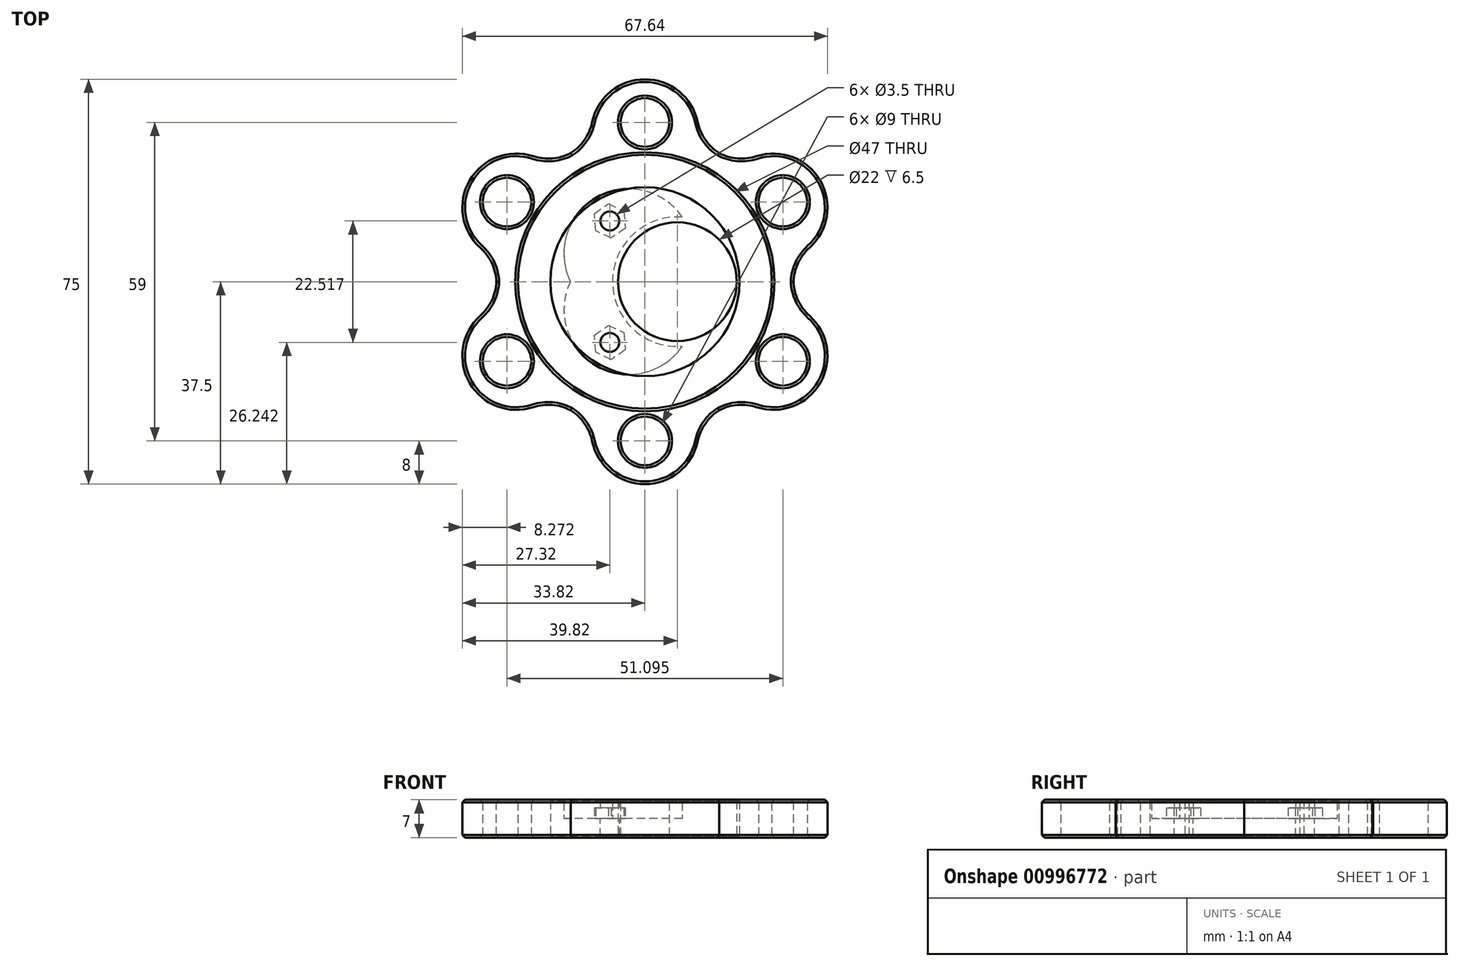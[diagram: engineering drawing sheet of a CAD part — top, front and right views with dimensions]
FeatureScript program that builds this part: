
annotation { "Feature Type Name" : "Feature", "Feature Type Description" : "" }
export const myFeature = defineFeature(function(context is Context, id is Id, definition is map)
    precondition{}
    {
        {
            var Q0;
            Q0=qCreatedBy(makeId("Top.planeOp"),FACE);
            var sketch = newSketch(context, id + "F0", { "sketchPlane" : qUnion([Q0])});
            skCircle(sketch, "E0", {"center": v(0, 0) * mm, "radius": 17.5 * mm});
            skCircle(sketch, "E1", {"center": v(6, 0) * mm, "radius": 11 * mm});
            skLineSegment(sketch, "E2", {"start": v(0, 0) * mm, "end": v(13.77, 19.66) * mm});
            skLineSegment(sketch, "E3", {"start": v(0, 0) * mm, "end": v(14.89, -21.26) * mm});
            skSolve(sketch);
        }
        {
            var Q0;
            Q0=qSketchRegion(id+"F0",true);
            var Q1;
            {var subQ0=sQuery(id+"F0.wireOp",EDGE,"7888d7e4-cc9e-4509-8198-0eb2202acd58");var subQ1=sQuery(id+"F0.wireOp",EDGE,"E0");var subQ2=makeQuery(id+"F0.imprint","INTERSECT",VERTEX,{"derivedFrom":[subQ1,subQ0]});Q1=makeQuery(id+"F0.imprint","IMPRINT",FACE,{"disambiguationData":[TD([[makeQuery(id+"F0.imprint","IMPRINT",EDGE,{"disambiguationData":[TD([[subQ2,1.0]])],"derivedFrom":subQ1}),1.0]])]});}
            extrude(context, id + "F1", {"entities" : qUnion([Q0, Q1]), "depth" : 3.25 * mm, "offsetDistance" : 25 * mm, "hasSecondDirection" : true, "secondDirectionOppositeDirection" : true, "secondDirectionDepth" : 3.25 * mm});
        }
        {
            var Q0;
            Q0=qCreatedBy(makeId("Top.planeOp"),FACE);
            var sketch = newSketch(context, id + "F2", { "sketchPlane" : qUnion([Q0])});
            skCircle(sketch, "E4", {"center": v(0, 0) * mm, "radius": 23.5 * mm});
            skArc(sketch, "E5", {"start": v(-3.88, 27.22) * mm, "mid": v(-13.75, 23.82) * mm, "end": v(-21.64, 16.97) * mm});
            skArc(sketch, "E6", {"start": v(9.83, 25.68) * mm, "mid": v(0, 37.5) * mm, "end": v(-9.83, 25.68) * mm});
            skArc(sketch, "E7.1.0", {"start": v(-17.32, 21.36) * mm, "mid": v(-32.48, 18.75) * mm, "end": v(-27.16, 4.33) * mm});
            skArc(sketch, "E7.2.0", {"start": v(-27.16, -4.33) * mm, "mid": v(-32.48, -18.75) * mm, "end": v(-17.32, -21.36) * mm});
            skArc(sketch, "E7.3.0", {"start": v(-9.83, -25.68) * mm, "mid": v(0, -37.5) * mm, "end": v(9.83, -25.68) * mm});
            skArc(sketch, "E7.4.0", {"start": v(17.32, -21.36) * mm, "mid": v(32.48, -18.75) * mm, "end": v(27.16, -4.33) * mm});
            skArc(sketch, "E7.5.0", {"start": v(27.16, 4.33) * mm, "mid": v(32.48, 18.75) * mm, "end": v(17.32, 21.36) * mm});
            skPoint(sketch, "E8.orphan", {"position": v(8.33, 21.97) * mm});
            skPoint(sketch, "E9.orphan", {"position": v(-8.33, 21.97) * mm});
            skPoint(sketch, "E10.orphan", {"position": v(-14.86, 18.2) * mm});
            skPoint(sketch, "E11.orphan", {"position": v(-23.2, 3.77) * mm});
            skPoint(sketch, "E12.orphan", {"position": v(-23.2, -3.77) * mm});
            skPoint(sketch, "E13.orphan", {"position": v(-14.86, -18.2) * mm});
            skPoint(sketch, "E14.orphan", {"position": v(-8.33, -21.97) * mm});
            skPoint(sketch, "E15.orphan", {"position": v(8.33, -21.97) * mm});
            skPoint(sketch, "E16.orphan", {"position": v(14.86, -18.2) * mm});
            skPoint(sketch, "E17.orphan", {"position": v(23.2, -3.77) * mm});
            skPoint(sketch, "E18.orphan", {"position": v(23.2, 3.77) * mm});
            skPoint(sketch, "E19.orphan", {"position": v(14.86, 18.2) * mm});
            skCircle(sketch, "E20", {"center": v(0, 29.5) * mm, "radius": 4.5 * mm});
            skCircle(sketch, "E21.1.0", {"center": v(-25.55, 14.75) * mm, "radius": 4.5 * mm});
            skCircle(sketch, "E21.2.0", {"center": v(-25.55, -14.75) * mm, "radius": 4.5 * mm});
            skCircle(sketch, "E21.3.0", {"center": v(0, -29.5) * mm, "radius": 4.5 * mm});
            skCircle(sketch, "E21.4.0", {"center": v(25.55, -14.75) * mm, "radius": 4.5 * mm});
            skCircle(sketch, "E21.5.0", {"center": v(25.55, 14.75) * mm, "radius": 4.5 * mm});
            skArc(sketch, "E22.trimOffspring", {"start": v(21.64, 16.97) * mm, "mid": v(13.75, 23.82) * mm, "end": v(3.88, 27.22) * mm});
            skArc(sketch, "E23.trimOffspring", {"start": v(25.52, -10.25) * mm, "mid": v(27.5, 0) * mm, "end": v(25.52, 10.25) * mm});
            skArc(sketch, "E24.trimOffspring", {"start": v(3.88, -27.22) * mm, "mid": v(13.75, -23.82) * mm, "end": v(21.64, -16.97) * mm});
            skArc(sketch, "E25.trimOffspring", {"start": v(-21.64, -16.97) * mm, "mid": v(-13.75, -23.82) * mm, "end": v(-3.88, -27.22) * mm});
            skArc(sketch, "E26.trimOffspring", {"start": v(-25.52, 10.25) * mm, "mid": v(-27.5, 0) * mm, "end": v(-25.52, -10.25) * mm});
            skSolve(sketch);
        }
        {
            var Q0;
            Q0=qSketchRegion(id+"F2",true);
            extrude(context, id + "F3", {"entities" : qUnion([Q0]), "depth" : 3.5 * mm, "offsetDistance" : 25 * mm, "hasSecondDirection" : true, "secondDirectionOppositeDirection" : true, "secondDirectionDepth" : 3.5 * mm});
        }
        {
            var Q0;
            {var subQ0=sQuery(id+"F2.wireOp",EDGE,"E7.1.0");var subQ1=sQuery(id+"F2.wireOp",EDGE,"E5");Q0=makeQuery(id+"F3.opExtrude","SWEPT_EDGE",EDGE,{"disambiguationData":[OSD([subQ1,subQ0]),TDD([makeQuery(id+"F2.imprint","INTERSECT",VERTEX,{"disambiguationData":[OD(0.0)],"derivedFrom":[subQ1,subQ0]})])]});}
            var Q1;
            {var subQ0=sQuery(id+"F2.wireOp",EDGE,"E6");var subQ1=sQuery(id+"F2.wireOp",EDGE,"E5");Q1=makeQuery(id+"F3.opExtrude","SWEPT_EDGE",EDGE,{"disambiguationData":[OSD([subQ1,subQ0]),TDD([makeQuery(id+"F2.imprint","INTERSECT",VERTEX,{"disambiguationData":[OD(1.0)],"derivedFrom":[subQ1,subQ0]})])]});}
            var Q2;
            {var subQ0=sQuery(id+"F2.wireOp",EDGE,"E7.1.0");var subQ1=sQuery(id+"F2.wireOp",EDGE,"E5");Q2=makeQuery(id+"F3.opExtrude","SWEPT_EDGE",EDGE,{"disambiguationData":[OSD([subQ1,subQ0]),TDD([makeQuery(id+"F2.imprint","INTERSECT",VERTEX,{"disambiguationData":[OD(1.0)],"derivedFrom":[subQ1,subQ0]})])]});}
            var Q3;
            {var subQ0=sQuery(id+"F2.wireOp",EDGE,"E7.2.0");var subQ1=sQuery(id+"F2.wireOp",EDGE,"E5");Q3=makeQuery(id+"F3.opExtrude","SWEPT_EDGE",EDGE,{"disambiguationData":[OSD([subQ1,subQ0]),TDD([makeQuery(id+"F2.imprint","INTERSECT",VERTEX,{"disambiguationData":[OD(0.0)],"derivedFrom":[subQ1,subQ0]})])]});}
            var Q4;
            {var subQ0=sQuery(id+"F2.wireOp",EDGE,"E7.2.0");var subQ1=sQuery(id+"F2.wireOp",EDGE,"E5");Q4=makeQuery(id+"F3.opExtrude","SWEPT_EDGE",EDGE,{"disambiguationData":[OSD([subQ1,subQ0]),TDD([makeQuery(id+"F2.imprint","INTERSECT",VERTEX,{"disambiguationData":[OD(1.0)],"derivedFrom":[subQ1,subQ0]})])]});}
            var Q5;
            {var subQ0=sQuery(id+"F2.wireOp",EDGE,"E7.3.0");var subQ1=sQuery(id+"F2.wireOp",EDGE,"E5");Q5=makeQuery(id+"F3.opExtrude","SWEPT_EDGE",EDGE,{"disambiguationData":[OSD([subQ1,subQ0]),TDD([makeQuery(id+"F2.imprint","INTERSECT",VERTEX,{"disambiguationData":[OD(0.0)],"derivedFrom":[subQ1,subQ0]})])]});}
            var Q6;
            {var subQ0=sQuery(id+"F2.wireOp",EDGE,"E7.3.0");var subQ1=sQuery(id+"F2.wireOp",EDGE,"E5");Q6=makeQuery(id+"F3.opExtrude","SWEPT_EDGE",EDGE,{"disambiguationData":[OSD([subQ1,subQ0]),TDD([makeQuery(id+"F2.imprint","INTERSECT",VERTEX,{"disambiguationData":[OD(1.0)],"derivedFrom":[subQ1,subQ0]})])]});}
            var Q7;
            {var subQ0=sQuery(id+"F2.wireOp",EDGE,"E7.4.0");var subQ1=sQuery(id+"F2.wireOp",EDGE,"E5");Q7=makeQuery(id+"F3.opExtrude","SWEPT_EDGE",EDGE,{"disambiguationData":[OSD([subQ1,subQ0]),TDD([makeQuery(id+"F2.imprint","INTERSECT",VERTEX,{"disambiguationData":[OD(0.0)],"derivedFrom":[subQ1,subQ0]})])]});}
            var Q8;
            {var subQ0=sQuery(id+"F2.wireOp",EDGE,"E7.4.0");var subQ1=sQuery(id+"F2.wireOp",EDGE,"E5");Q8=makeQuery(id+"F3.opExtrude","SWEPT_EDGE",EDGE,{"disambiguationData":[OSD([subQ1,subQ0]),TDD([makeQuery(id+"F2.imprint","INTERSECT",VERTEX,{"disambiguationData":[OD(1.0)],"derivedFrom":[subQ1,subQ0]})])]});}
            var Q9;
            {var subQ0=sQuery(id+"F2.wireOp",EDGE,"E7.5.0");var subQ1=sQuery(id+"F2.wireOp",EDGE,"E5");Q9=makeQuery(id+"F3.opExtrude","SWEPT_EDGE",EDGE,{"disambiguationData":[OSD([subQ1,subQ0]),TDD([makeQuery(id+"F2.imprint","INTERSECT",VERTEX,{"disambiguationData":[OD(0.0)],"derivedFrom":[subQ1,subQ0]})])]});}
            var Q10;
            {var subQ0=sQuery(id+"F2.wireOp",EDGE,"E7.5.0");var subQ1=sQuery(id+"F2.wireOp",EDGE,"E5");Q10=makeQuery(id+"F3.opExtrude","SWEPT_EDGE",EDGE,{"disambiguationData":[OSD([subQ1,subQ0]),TDD([makeQuery(id+"F2.imprint","INTERSECT",VERTEX,{"disambiguationData":[OD(1.0)],"derivedFrom":[subQ1,subQ0]})])]});}
            var Q11;
            {var subQ0=sQuery(id+"F2.wireOp",EDGE,"E6");var subQ1=sQuery(id+"F2.wireOp",EDGE,"E5");Q11=makeQuery(id+"F3.opExtrude","SWEPT_EDGE",EDGE,{"disambiguationData":[OSD([subQ1,subQ0]),TDD([makeQuery(id+"F2.imprint","INTERSECT",VERTEX,{"disambiguationData":[OD(0.0)],"derivedFrom":[subQ1,subQ0]})])]});}
            var Q12;
            Q12=makeQuery(id+"F3.opExtrude","SWEPT_EDGE",EDGE,{"disambiguationData":[OSD([sQuery(id+"F2.wireOp",EDGE,"E7.1.0"),sQuery(id+"F2.wireOp",EDGE,"E26.trimOffspring")])]});
            var Q13;
            Q13=makeQuery(id+"F3.opExtrude","SWEPT_EDGE",EDGE,{"disambiguationData":[OSD([sQuery(id+"F2.wireOp",EDGE,"E6"),sQuery(id+"F2.wireOp",EDGE,"E22.trimOffspring")])]});
            fillet(context, id + "F4", {"entities" : qUnion([Q0, Q1, Q2, Q3, Q4, Q5, Q6, Q7, Q8, Q9, Q10, Q11, Q12, Q13]), "tangentPropagation" : true, "radius" : 9 * mm, "defaultsChanged" : false, "vertexSettings" : [], "allowEdgeOverflow" : false});
        }
        {
            var Q0;
            Q0=qCreatedBy(makeId("Top.planeOp"),FACE);
            var sketch = newSketch(context, id + "F5", { "sketchPlane" : qUnion([Q0])});
            skLineSegment(sketch, "E27", {"start": v(0, -24.5) * mm, "end": v(35, 0) * mm});
            skLineSegment(sketch, "E28", {"start": v(35, 0) * mm, "end": v(0, 24.5) * mm});
            skSolve(sketch);
        }
        {
            var Q0;
            Q0=qSketchRegion(id+"F5",true);
            var Q1;
            Q1=sQuery(id+"F5.wireOp",EDGE,"E28");
            var Q2;
            Q2=sQuery(id+"F5.wireOp",EDGE,"E27");
            extrude(context, id + "F6", {"entities" : qUnion([Q0]), "bodyType" : ToolBodyType.SURFACE, "surfaceEntities" : qUnion([Q1, Q2]), "depth" : 3.5 * mm, "offsetDistance" : 25 * mm, "hasSecondDirection" : true, "secondDirectionOppositeDirection" : true, "secondDirectionDepth" : 3.5 * mm});
        }
        {
            var Q0;
            Q0=makeQuery(id+"F6.opExtrude","SWEPT_FACE",FACE,{"disambiguationData":[OSD([sQuery(id+"F5.wireOp",EDGE,"E28")])]});
            var sketch = newSketch(context, id + "F7", { "sketchPlane" : qUnion([Q0])});
            skPoint(sketch, "E29", {"position": v(0, 0) * mm});
            skSolve(sketch);
        }
        {
            var Q0;
            Q0=makeQuery(id+"F6.opExtrude","SWEPT_FACE",FACE,{"disambiguationData":[OSD([sQuery(id+"F5.wireOp",EDGE,"E27")])]});
            var sketch = newSketch(context, id + "F8", { "sketchPlane" : qUnion([Q0])});
            skPoint(sketch, "E30", {"position": v(0, 0) * mm});
            skSolve(sketch);
        }
        {
            var Q0;
            Q0=qCreatedBy(makeId("Top.planeOp"),FACE);
            var sketch = newSketch(context, id + "F9", { "sketchPlane" : qUnion([Q0])});
            skArc(sketch, "E31", {"start": v(6.9, 11.97) * mm, "mid": v(-6, 0) * mm, "end": v(6.9, -11.97) * mm});
            skArc(sketch, "E32.1.0", {"start": v(6.9, 11.97) * mm, "mid": v(-9, 15.59) * mm, "end": v(-13.82, 0) * mm});
            skArc(sketch, "E32.2.0", {"start": v(-13.82, 0) * mm, "mid": v(-9, -15.59) * mm, "end": v(6.9, -11.97) * mm});
            skPoint(sketch, "E32.center", {"position": v(0, 0) * mm});
            skLineSegment(sketch, "E33", {"start": v(-6.5, -11.26) * mm, "end": v(-3.9, -6.77) * mm});
            skLineSegment(sketch, "E34", {"start": v(-6.5, 11.26) * mm, "end": v(-3.9, 6.77) * mm});
            skSolve(sketch);
        }
        {
            var Q0;
            {var subQ0=sQuery(id+"F9.wireOp",EDGE,"E32.1.0");Q0=makeQuery(id+"F9.imprint","IMPRINT",FACE,{"disambiguationData":[TD([[makeQuery(id+"F9.imprint","IMPRINT",EDGE,{"derivedFrom":subQ0}),1.0]])]});}
            extrude(context, id + "F10", {"entities" : qUnion([Q0]), "depth" : 3 * mm, "offsetDistance" : 25 * mm});
        }
        {
            var Q0;
            {var subQ0=sQuery(id+"F9.wireOp",EDGE,"E32.1.0");Q0=makeQuery(id+"F9.imprint","IMPRINT",FACE,{"disambiguationData":[TD([[makeQuery(id+"F9.imprint","IMPRINT",EDGE,{"derivedFrom":subQ0}),1.0]])]});}
            var sketch = newSketch(context, id + "F11", { "sketchPlane" : qUnion([Q0])});
            skCircle(sketch, "E35.cCircle", {"center": v(-6.5, 11.26) * mm, "radius": 2.75 * mm, "construction": true});
            skLineSegment(sketch, "E35.0", {"start": v(-3.9, 13.07) * mm, "end": v(-3.63, 9.9) * mm});
            skLineSegment(sketch, "E35.1", {"start": v(-3.63, 9.9) * mm, "end": v(-6.24, 8.1) * mm});
            skLineSegment(sketch, "E35.2", {"start": v(-6.24, 8.1) * mm, "end": v(-9.1, 9.45) * mm});
            skLineSegment(sketch, "E35.3", {"start": v(-9.1, 9.45) * mm, "end": v(-9.37, 12.61) * mm});
            skLineSegment(sketch, "E35.4", {"start": v(-9.37, 12.61) * mm, "end": v(-6.76, 14.42) * mm});
            skLineSegment(sketch, "E35.5", {"start": v(-6.76, 14.42) * mm, "end": v(-3.9, 13.07) * mm});
            skPoint(sketch, "E35.0.midPoint", {"position": v(-3.76, 11.49) * mm});
            skCircle(sketch, "E36.cCircle", {"center": v(-6.5, -11.26) * mm, "radius": 2.75 * mm, "construction": true});
            skLineSegment(sketch, "E36.0", {"start": v(-3.9, -9.45) * mm, "end": v(-3.63, -12.61) * mm});
            skLineSegment(sketch, "E36.1", {"start": v(-3.63, -12.61) * mm, "end": v(-6.24, -14.42) * mm});
            skLineSegment(sketch, "E36.2", {"start": v(-6.24, -14.42) * mm, "end": v(-9.1, -13.07) * mm});
            skLineSegment(sketch, "E36.3", {"start": v(-9.1, -13.07) * mm, "end": v(-9.37, -9.9) * mm});
            skLineSegment(sketch, "E36.4", {"start": v(-9.37, -9.9) * mm, "end": v(-6.76, -8.1) * mm});
            skLineSegment(sketch, "E36.5", {"start": v(-6.76, -8.1) * mm, "end": v(-3.9, -9.45) * mm});
            skPoint(sketch, "E36.0.midPoint", {"position": v(-3.76, -11.03) * mm});
            skSolve(sketch);
        }
        {
            var Q0;
            Q0 = qSketchRegion(id + "F11", true);
            extrude(context, id + "F12", {"entities" : qUnion([Q0]), "operationType" : NewBodyOperationType.REMOVE, "depth" : 2 * mm, "offsetDistance" : 25 * mm});
        }
        {
            var Q0;
            {var subQ0=sQuery(id+"F9.wireOp",EDGE,"E32.1.0");Q0=makeQuery(id+"F9.imprint","IMPRINT",FACE,{"disambiguationData":[TD([[makeQuery(id+"F9.imprint","IMPRINT",EDGE,{"derivedFrom":subQ0}),1.0]])]});}
            var sketch = newSketch(context, id + "F13", { "sketchPlane" : qUnion([Q0])});
            skCircle(sketch, "E37", {"center": v(-6.5, 11.26) * mm, "radius": 1.75 * mm});
            skCircle(sketch, "E38", {"center": v(-6.5, -11.26) * mm, "radius": 1.75 * mm});
            skSolve(sketch);
        }
        {
            var Q0;
            Q0 = qSketchRegion(id + "F13", true);
            extrude(context, id + "F14", {"entities" : qUnion([Q0]), "operationType" : NewBodyOperationType.REMOVE, "depth" : 25 * mm, "offsetDistance" : 25 * mm});
        }
        {
            var Q0;
            Q0=makeQuery(id+"F1.opExtrude","CAP_FACE",FACE,{"disambiguationData":[OSD([sQuery(id+"F0.wireOp",EDGE,"E0"),sQuery(id+"F0.wireOp",EDGE,"E1")])],"isStart":false});
            var sketch = newSketch(context, id + "F15", { "sketchPlane" : qUnion([Q0])});
            skCircle(sketch, "E39", {"center": v(-6.5, -11.26) * mm, "radius": 1.75 * mm});
            skCircle(sketch, "E40", {"center": v(-6.5, 11.26) * mm, "radius": 1.75 * mm});
            skSolve(sketch);
        }
        {
            var Q0;
            Q0 = qSketchRegion(id + "F15", true);
            extrude(context, id + "F16", {"entities" : qUnion([Q0]), "operationType" : NewBodyOperationType.REMOVE, "endBound" : BoundingType.THROUGH_ALL, "oppositeDirection" : true, "depth" : 25 * mm, "offsetDistance" : 25 * mm});
        }
        {
            var Q0;
            Q0=makeQuery(id+"F3.opExtrude","CAP_FACE",FACE,{"disambiguationData":[OSD([sQuery(id+"F2.wireOp",EDGE,"E4"),sQuery(id+"F2.wireOp",EDGE,"E5"),sQuery(id+"F2.wireOp",EDGE,"E6"),sQuery(id+"F2.wireOp",EDGE,"E7.1.0"),sQuery(id+"F2.wireOp",EDGE,"E7.2.0"),sQuery(id+"F2.wireOp",EDGE,"E7.3.0"),sQuery(id+"F2.wireOp",EDGE,"E7.4.0"),sQuery(id+"F2.wireOp",EDGE,"E7.5.0")])],"isStart":true});
            var Q1;
            Q1=makeQuery(id+"F3.opExtrude","CAP_FACE",FACE,{"disambiguationData":[OSD([sQuery(id+"F2.wireOp",EDGE,"E4"),sQuery(id+"F2.wireOp",EDGE,"E5"),sQuery(id+"F2.wireOp",EDGE,"E6"),sQuery(id+"F2.wireOp",EDGE,"E7.1.0"),sQuery(id+"F2.wireOp",EDGE,"E7.2.0"),sQuery(id+"F2.wireOp",EDGE,"E7.3.0"),sQuery(id+"F2.wireOp",EDGE,"E7.4.0"),sQuery(id+"F2.wireOp",EDGE,"E7.5.0")])],"isStart":false});
            chamfer(context, id + "F17", {"entities" : qUnion([Q0, Q1]), "width" : 0.5 * mm, "tangentPropagation" : true});
        }
    });
